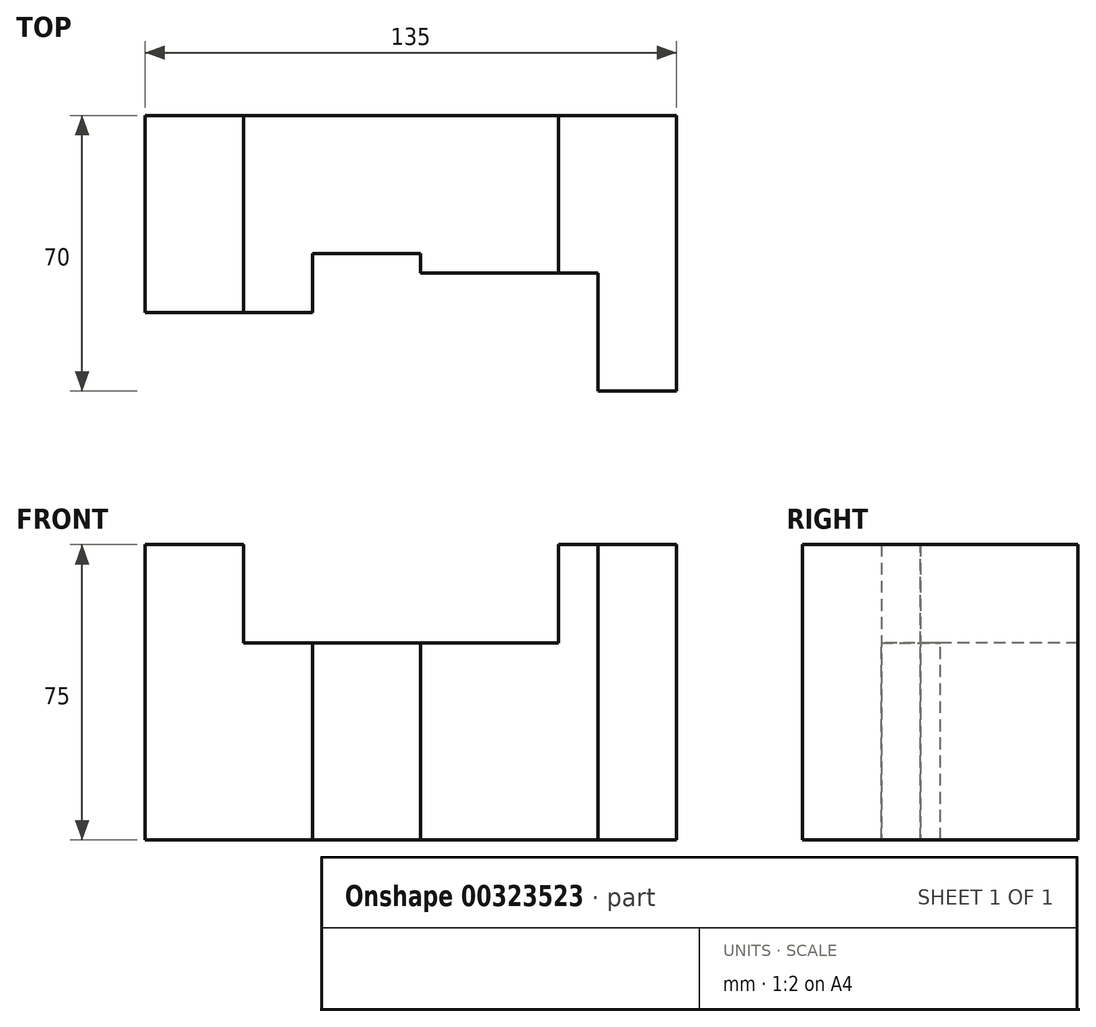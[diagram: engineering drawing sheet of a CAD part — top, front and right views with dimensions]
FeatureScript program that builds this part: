
annotation { "Feature Type Name" : "Feature", "Feature Type Description" : "" }
export const myFeature = defineFeature(function(context is Context, id is Id, definition is map)
    precondition{}
    {
        {
            var Q0;
            Q0=qCreatedBy(makeId("Top.planeOp"),FACE);
            var sketch = newSketch(context, id + "F0", { "sketchPlane" : qUnion([Q0])});
            skLineSegment(sketch, "E0", {"start": v(0, 0) * mm, "end": v(0, 50) * mm});
            skLineSegment(sketch, "E1", {"start": v(0, 50) * mm, "end": v(25, 50) * mm});
            skLineSegment(sketch, "E2", {"start": v(25, 50) * mm, "end": v(25, 0) * mm});
            skLineSegment(sketch, "E3", {"start": v(25, 0) * mm, "end": v(0, 0) * mm});
            skSolve(sketch);
        }
        {
            var Q0;
            Q0=makeQuery(id+"F0.imprint","IMPRINT",FACE,{"disambiguationData":[TD([[makeQuery(id+"F0.imprint","IMPRINT",EDGE,{"derivedFrom":sQuery(id+"F0.wireOp",EDGE,"E0")}),-1.0]])]});
            extrude(context, id + "F1", {"entities" : qUnion([Q0]), "depth" : 75 * mm});
        }
        {
            var Q0;
            Q0=makeQuery(id+"F1.opExtrude","CAP_FACE",FACE,{"disambiguationData":[OSD([sQuery(id+"F0.wireOp",EDGE,"E0"),sQuery(id+"F0.wireOp",EDGE,"E1"),sQuery(id+"F0.wireOp",EDGE,"E2"),sQuery(id+"F0.wireOp",EDGE,"E3")])],"isStart":false});
            var sketch = newSketch(context, id + "F2", { "sketchPlane" : qUnion([Q0])});
            skLineSegment(sketch, "E4", {"start": v(25, 0) * mm, "end": v(42.5, 0) * mm});
            skLineSegment(sketch, "E5", {"start": v(42.5, 0) * mm, "end": v(42.5, 15) * mm});
            skLineSegment(sketch, "E6", {"start": v(42.5, 15) * mm, "end": v(70, 15) * mm});
            skLineSegment(sketch, "E7", {"start": v(70, 15) * mm, "end": v(70, 10) * mm});
            skLineSegment(sketch, "E8", {"start": v(70, 10) * mm, "end": v(105, 10) * mm});
            skLineSegment(sketch, "E9", {"start": v(105, 10) * mm, "end": v(105, 50) * mm});
            skLineSegment(sketch, "E10", {"start": v(105, 50) * mm, "end": v(25, 50) * mm});
            skLineSegment(sketch, "E11", {"start": v(25, 50) * mm, "end": v(25, 0) * mm});
            skSolve(sketch);
        }
        {
            var Q0;
            Q0=makeQuery(id+"F2.imprint","IMPRINT",FACE,{"disambiguationData":[TD([[makeQuery(id+"F2.imprint","IMPRINT",EDGE,{"derivedFrom":sQuery(id+"F2.wireOp",EDGE,"E4")}),1.0]])]});
            extrude(context, id + "F3", {"entities" : qUnion([Q0]), "operationType" : NewBodyOperationType.ADD, "oppositeDirection" : true, "depth" : 75 * mm});
        }
        {
            var Q0;
            Q0=makeQuery(id+"F3.boolean.opBoolean","MERGE",FACE,{"derivedFrom":[makeQuery(id+"F1.opExtrude","CAP_FACE",FACE,{"disambiguationData":[OSD([sQuery(id+"F0.wireOp",EDGE,"E0"),sQuery(id+"F0.wireOp",EDGE,"E1"),sQuery(id+"F0.wireOp",EDGE,"E2"),sQuery(id+"F0.wireOp",EDGE,"E3")])],"isStart":false}),makeQuery(id+"F3.opExtrude","CAP_FACE",FACE,{"disambiguationData":[OSD([sQuery(id+"F2.wireOp",EDGE,"E4"),sQuery(id+"F2.wireOp",EDGE,"E5"),sQuery(id+"F2.wireOp",EDGE,"E6"),sQuery(id+"F2.wireOp",EDGE,"E7"),sQuery(id+"F2.wireOp",EDGE,"E8"),sQuery(id+"F2.wireOp",EDGE,"E9"),sQuery(id+"F2.wireOp",EDGE,"E10"),sQuery(id+"F2.wireOp",EDGE,"E11")])],"isStart":true})]});
            var sketch = newSketch(context, id + "F4", { "sketchPlane" : qUnion([Q0])});
            skLineSegment(sketch, "E12", {"start": v(105, 50) * mm, "end": v(135, 50) * mm});
            skLineSegment(sketch, "E13", {"start": v(135, 50) * mm, "end": v(135, -20) * mm});
            skLineSegment(sketch, "E14", {"start": v(135, -20) * mm, "end": v(105, -20) * mm});
            skLineSegment(sketch, "E15", {"start": v(105, -20) * mm, "end": v(105, 50) * mm});
            skSolve(sketch);
        }
        {
            var Q0;
            {var subQ3=sQuery(id+"F4.wireOp",EDGE,"E12");Q0=makeQuery(id+"F4.imprint","IMPRINT",FACE,{"disambiguationData":[TD([[makeQuery(id+"F4.imprint","IMPRINT",EDGE,{"derivedFrom":subQ3}),-1.0]])]});}
            extrude(context, id + "F5", {"entities" : qUnion([Q0]), "operationType" : NewBodyOperationType.ADD, "oppositeDirection" : true, "depth" : 75 * mm});
        }
        {
            var Q0;
            Q0=makeQuery(id+"F5.opExtrude","SWEPT_FACE",FACE,{"disambiguationData":[OSD([sQuery(id+"F4.wireOp",EDGE,"E14")])]});
            var sketch = newSketch(context, id + "F6", { "sketchPlane" : qUnion([Q0])});
            skLineSegment(sketch, "E16", {"start": v(135, 75) * mm, "end": v(105, 75) * mm});
            skLineSegment(sketch, "E17", {"start": v(105, 75) * mm, "end": v(25, 75) * mm});
            skLineSegment(sketch, "E18", {"start": v(25, 75) * mm, "end": v(25, 50) * mm});
            skLineSegment(sketch, "E19", {"start": v(25, 50) * mm, "end": v(105, 50) * mm});
            skLineSegment(sketch, "E20", {"start": v(105, 50) * mm, "end": v(105, 75) * mm});
            skSolve(sketch);
        }
        {
            var Q0;
            Q0=makeQuery(id+"F6.imprint","IMPRINT",FACE,{"disambiguationData":[TD([[makeQuery(id+"F6.imprint","IMPRINT",EDGE,{"derivedFrom":sQuery(id+"F6.wireOp",EDGE,"E17")}),1.0]])]});
            extrude(context, id + "F7", {"entities" : qUnion([Q0]), "operationType" : NewBodyOperationType.REMOVE, "oppositeDirection" : true, "depth" : 75 * mm});
        }
        {
            var Q0;
            Q0=makeQuery(id+"F5.opExtrude","SWEPT_FACE",FACE,{"disambiguationData":[OSD([sQuery(id+"F4.wireOp",EDGE,"E14")])]});
            var sketch = newSketch(context, id + "F8", { "sketchPlane" : qUnion([Q0])});
            skLineSegment(sketch, "E21", {"start": v(105, 75) * mm, "end": v(115, 75) * mm});
            skLineSegment(sketch, "E22", {"start": v(115, 75) * mm, "end": v(115, 0) * mm});
            skLineSegment(sketch, "E23", {"start": v(115, 0) * mm, "end": v(105, 0) * mm});
            skLineSegment(sketch, "E24", {"start": v(105, 0) * mm, "end": v(105, 75) * mm});
            skSolve(sketch);
        }
        {
            var Q0;
            Q0=makeQuery(id+"F8.imprint","IMPRINT",FACE,{"disambiguationData":[TD([[makeQuery(id+"F8.imprint","IMPRINT",EDGE,{"derivedFrom":sQuery(id+"F8.wireOp",EDGE,"E21")}),1.0]])]});
            extrude(context, id + "F9", {"entities" : qUnion([Q0]), "operationType" : NewBodyOperationType.REMOVE, "oppositeDirection" : true, "depth" : 30 * mm});
        }
    });
